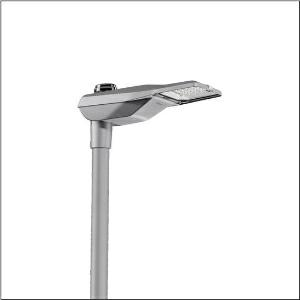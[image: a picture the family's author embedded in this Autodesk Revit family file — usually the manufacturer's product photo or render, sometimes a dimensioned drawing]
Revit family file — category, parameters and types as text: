
# Revit family: streetlight_sl_21_micro___stw1_0a_5xe5e37n08cb_b20b
name_source: partatom
category: Lighting Fixtures
units: mm (PartAtom-declared; Revit-internal decimal feet)

## family parameters
Cut with Voids When Loaded = No
Host = Face
Light Source = No
Part Type = Normal
Room Calculation Point = No
Round Connector Dimension = Use Diameter
Shared = No

## types (1)
- --- (1 x LED, 2290 lm, 15.8 W, 3000K)
    Apparent Load = 16 VA
    CIE Flux Codes = 38 75 98 100 100
    Color Rendering = 70
    Color Temperature = 3000K
    Default Elevation = 1800 mm
    Description = Streetlight SL 21 micro, mast luminaire, primary light control with lens, of PMMA, primary optical cover: cover, of toughened safety glass, transparent, light distribution: STW1.0a, light emission: direct distribution, primary light characteristic: asymmetric, installation type: post-top, LED, 3G 1.5mm², High Power LED, rated luminous flux: 2.290lm, luminous efficacy: 145lm/W, light colour: 730, colour temperature: 3000K, control: overheat protection, pre-setting: linear dimming characteristic, constant luminous flux control, time-dependent luminous flux control, flexible luminous flux parameterisation, mains connection: 230..240V, AC, 50/60Hz, connection cable pre-assembled, cable length: 6,5m, wiring characteristics: H07RN-F, start of lifetime: 16W, end of service life: 16W, reduction: 8W, luminaire housing, of diecast aluminium (EN AC-44300), powder-coated, Siteco® metallic grey (DB 702S), corrosivity category C5 mid according to DIN EN ISO 12944, multi-level sealing system, sealing non-destructively replaceable, inclination adjustable: 0°, 5°, 10°, 15°, length: 528mm, width: 235mm, height: 110mm, spigot size: 76/60mm (post-top), protection rating (complete): IP66, insulation class (complete): insulation class I (protective earthing), certification: CE, ENEC, ENEC+, VDE, impact resistance: IK09, permissible operating ambient temperature for outdoor applications: -40..+50°C, standard-compliant lighting for roads and squares, packaging unit: 1 piece

Light Distribution: STW1.0a
    Height = 110 mm
    Lamp = 1 x LED
    Lamp Light Flux = 2290 lm
    Lamp Power = 15.8 W
    Lamp count = 1
    Length = 528 mm
    Luminous efficacy = 145 lm/W
    Manufacturer = Siteco
    ModVariant = No
    Model = 5XE5E37N08CB
    Number of Poles = 1
    OnlyDefault = Yes
    Power Factor = 1
    Product Name = Streetlight SL 21 micro | STW1.0a
    Product group = mast luminaire | pylon top
    ProductGroupID = 6100
    Protection Class = Protection class I
    Protection Degree = IP 66
    RLX_Detail_Level = 1
    RLX_Emergency_Light_Flux = 0 lm
    RLX_Emergency_Type = 0
    RLX_Emergency_Type_DB = No
    RlxData = <blob elided: 97929 chars, md5=aca7360d>
    Socket = socket
    Standby Power = 0 W
    System Light Flux = 2290 lm
    System Power = 16 W
    Type Comments = factory setting: luminous flux: 100 % | dim-lin: 254 | 300 mA
    Type Image = l_1294375.jpg
    URL = http://relux.com
    VarID = @adj_105665
    Voltage = 0 V
    Weight = 0.00 kg
    Width = 235 mm

## geometry (parser evidence)
native form markers: Blend x4, Sweep x9
no freeform markers — native parametric forms only
